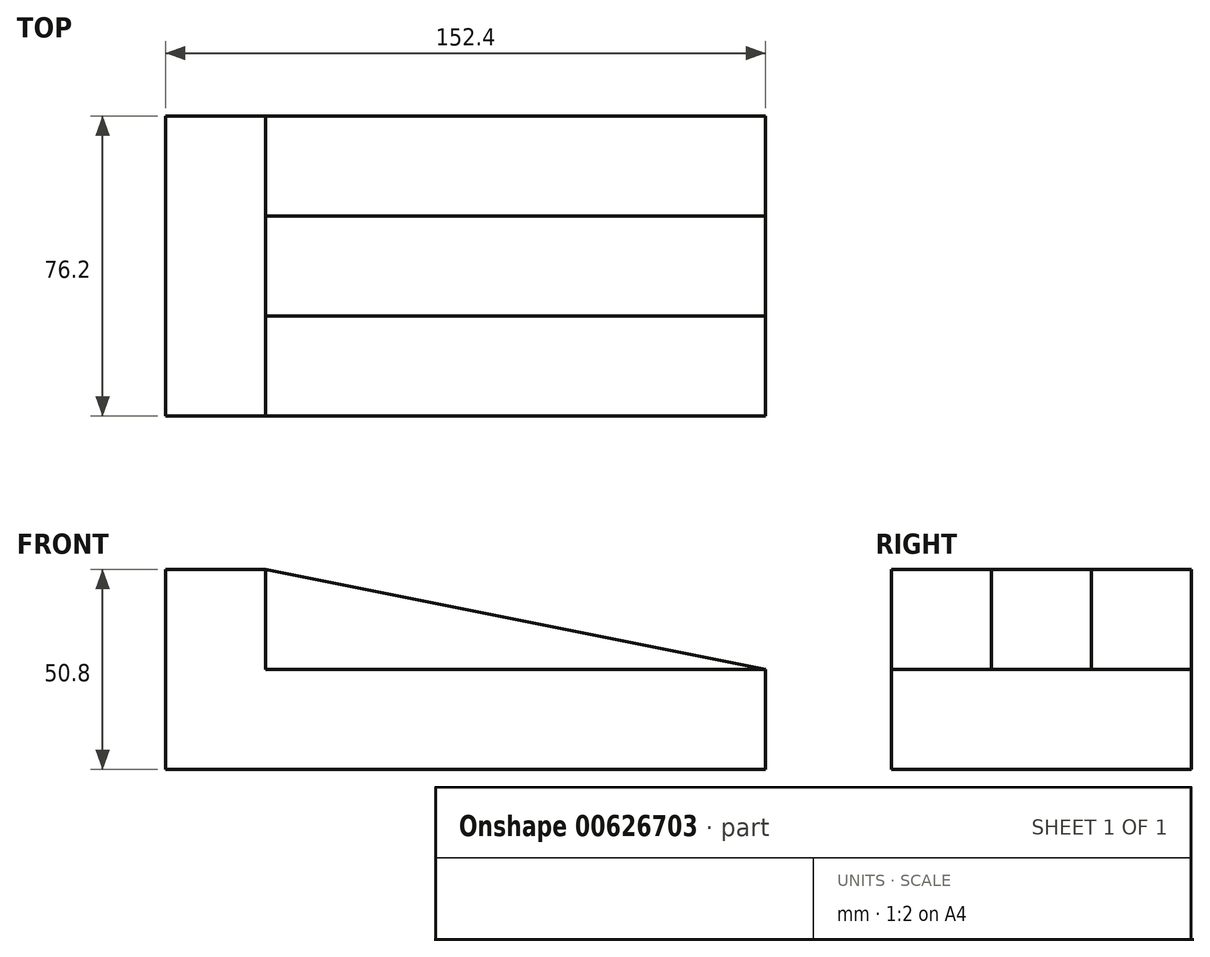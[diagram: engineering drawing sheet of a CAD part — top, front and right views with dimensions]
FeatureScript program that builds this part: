
annotation { "Feature Type Name" : "Feature", "Feature Type Description" : "" }
export const myFeature = defineFeature(function(context is Context, id is Id, definition is map)
    precondition{}
    {
        {
            var Q0;
            Q0=qCreatedBy(makeId("Front.planeOp"),FACE);
            var sketch = newSketch(context, id + "F0", { "sketchPlane" : qUnion([Q0])});
            skLineSegment(sketch, "E0", {"start": v(-76.58, 0) * mm, "end": v(75.82, 0) * mm});
            skLineSegment(sketch, "E1", {"start": v(75.82, 0) * mm, "end": v(75.82, 25.4) * mm});
            skLineSegment(sketch, "E2", {"start": v(75.82, 25.4) * mm, "end": v(-51.18, 25.4) * mm});
            skLineSegment(sketch, "E3", {"start": v(-51.18, 25.4) * mm, "end": v(-51.18, 50.8) * mm});
            skLineSegment(sketch, "E4", {"start": v(-51.18, 50.8) * mm, "end": v(-76.58, 50.8) * mm});
            skLineSegment(sketch, "E5", {"start": v(-76.58, 50.8) * mm, "end": v(-76.58, 0) * mm});
            skSolve(sketch);
        }
        {
            var Q0;
            Q0 = qSketchRegion(id + "F0", true);
            extrude(context, id + "F1", {"entities" : qUnion([Q0]), "oppositeDirection" : true, "depth" : 76.2 * mm, "offsetDistance" : 25.4 * mm});
        }
        {
            var Q0;
            Q0=makeQuery(id+"F1.opExtrude","SWEPT_FACE",FACE,{"disambiguationData":[OSD([sQuery(id+"F0.wireOp",EDGE,"E2")])]});
            var sketch = newSketch(context, id + "F2", { "sketchPlane" : qUnion([Q0])});
            skLineSegment(sketch, "E6", {"start": v(75.82, 25.4) * mm, "end": v(-51.18, 25.4) * mm});
            skLineSegment(sketch, "E7", {"start": v(75.82, 50.8) * mm, "end": v(-51.18, 50.8) * mm});
            skSolve(sketch);
        }
        {
            var Q0;
            Q0 = qSketchRegion(id + "F2", true);
            var Q1;
            {var subQ0=sQuery(id+"F2.wireOp",EDGE,"E6");Q1=makeQuery(id+"F2.imprint","IMPRINT",FACE,{"disambiguationData":[TD([[makeQuery(id+"F2.imprint","IMPRINT",EDGE,{"derivedFrom":subQ0}),-1.0]])]});}
            extrude(context, id + "F3", {"entities" : qUnion([Q0, Q1]), "operationType" : NewBodyOperationType.ADD, "depth" : 25.4 * mm, "offsetDistance" : 25.4 * mm});
        }
        {
            var Q0;
            Q0=makeQuery(id+"F3.opExtrude","SWEPT_FACE",FACE,{"disambiguationData":[OSD([sQuery(id+"F2.wireOp",EDGE,"E6")])]});
            var sketch = newSketch(context, id + "F4", { "sketchPlane" : qUnion([Q0])});
            skLineSegment(sketch, "E8", {"start": v(-51.18, 50.8) * mm, "end": v(75.82, 25.4) * mm});
            skSolve(sketch);
        }
        {
            var Q0;
            Q0 = qSketchRegion(id + "F4", true);
            var Q1;
            Q1=makeQuery(id+"F4.imprint","IMPRINT",FACE,{"disambiguationData":[TD([[makeQuery(id+"F4.imprint","IMPRINT",EDGE,{"derivedFrom":sQuery(id+"F4.wireOp",EDGE,"E8")}),1.0]])]});
            extrude(context, id + "F5", {"entities" : qUnion([Q0, Q1]), "operationType" : NewBodyOperationType.REMOVE, "oppositeDirection" : true, "depth" : 25.4 * mm, "offsetDistance" : 25.4 * mm});
        }
    });
